# Revit family: HL_RU_Roof drain_HL80.3-B-221103
name_source: partatom
category: Instalační zařizovací předměty
units: mm (PartAtom-declared; Revit-internal decimal feet)

## family parameters
Bod výpočtu místnosti = Ano
Kóta kulaté spojky = Použít průměr
Nadpis OmniClass = Deck Waste Water Drains
Ořezat dutým tvarem při načtení = Ne
Sdílené = Ne
Typ dílu = Normální
Vždy vertikální = Ano
Založené na pracovní rovině = Ne
Číslo OmniClass = 23.70.50.21.24.14

## types (1)
- HL_Кровельная воронка_HL80.3
    EAN = 9003076908035
    Indexovaná poznámka = HL80.3
    Komentáře k typům = HL80.3 Трап для кровли DN50/75 поворотный с листвоуловителем.,
    Model = HL80.3
    Popis = Кровельные воронки
    Přípoj CW = Ne
    Přípoj HW = Ne
    Přípoj odpadních dílů = Ano
    Přípoj ventilace = Ne
    URL = http://www.hutterer-lechner.com
    Výchozí výška = 0 mm  [stored 0 ft]
    Výrobce = HL Hutterer & Lechner GmbH
    ВЕС = 0,37 [kg]
    ВЫСОТА МОНТАЖА = 91 mm
    МАТЕРИАЛ = PP/PE
    ПРОИЗВОДИТЕЛЬНОСТЬ = 1,0 l/s
    РАЗМЕР = DN50/75
    РЕШЁТКА = Laubfangkorb d 110 mm

note: [stored X ft] marks values corroborated as IEEE doubles in the binary element streams (Revit-internal decimal feet)

## geometry (parser evidence)
native form markers: Sweep x21
no freeform markers — native parametric forms only
